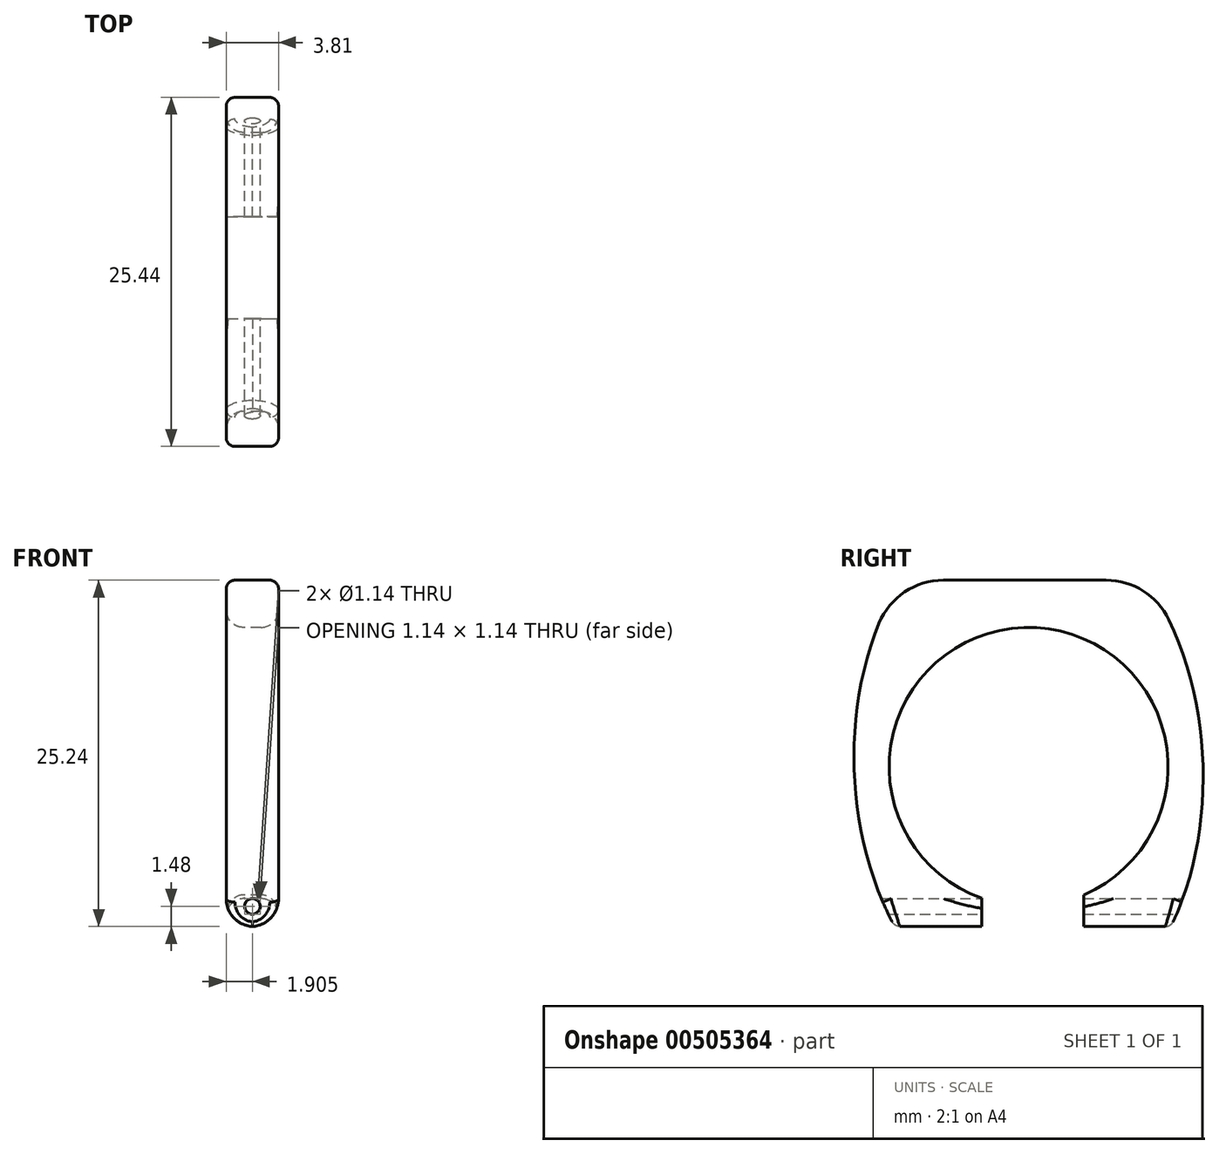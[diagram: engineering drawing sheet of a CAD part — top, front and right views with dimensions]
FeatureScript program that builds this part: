
annotation { "Feature Type Name" : "Feature", "Feature Type Description" : "" }
export const myFeature = defineFeature(function(context is Context, id is Id, definition is map)
    precondition{}
    {
        {
            var Q0;
            Q0=qCreatedBy(makeId("Right.planeOp"),FACE);
            var sketch = newSketch(context, id + "F0", { "sketchPlane" : qUnion([Q0])});
            skCircle(sketch, "E0", {"center": v(0, 10.16) * mm, "radius": 10.16 * mm});
            skEllipticalArc(sketch, "E1", {});
            skLineSegment(sketch, "E2", {"start": v(10.36, -1.48) * mm, "end": v(4.01, -1.48) * mm});
            skLineSegment(sketch, "E3", {"start": v(8.53, 23.76) * mm, "end": v(-9.25, 23.76) * mm});
            skCircle(sketch, "E4", {"center": v(0, 10.16) * mm, "radius": 0.64 * mm});
            skPoint(sketch, "E5", {"position": v(4.01, -1.48) * mm});
            skPoint(sketch, "E6", {"position": v(-3.4, -1.48) * mm});
            skLineSegment(sketch, "E7.trimOffspring", {"start": v(-3.4, -1.48) * mm, "end": v(-9.75, -1.48) * mm});
            skLineSegment(sketch, "E8", {"start": v(4.01, -1.48) * mm, "end": v(4.01, 0.83) * mm});
            skLineSegment(sketch, "E9", {"start": v(-3.4, -1.48) * mm, "end": v(-3.4, 0.59) * mm});
            const initialGuessF0  = {"E1": [0, 0.01016, -0.047142897118615544, 0.9988881555265653, 0.01905, 0.0127, 4.023068995079654, 2.197209903459385]};
            skSetInitialGuess(sketch, initialGuessF0);
            skSolve(sketch);
        }
        {
            var Q0;
            Q0=makeQuery(id+"F0.imprint","IMPRINT",FACE,{"disambiguationData":[TD([[makeQuery(id+"F0.imprint","IMPRINT",EDGE,{"derivedFrom":sQuery(id+"F0.wireOp",EDGE,"E0")}),-1.0]])]});
            extrude(context, id + "F1", {"entities" : qUnion([Q0]), "depth" : 3.8 * mm});
        }
        {
            var Q0;
            Q0=makeQuery(id+"F1.opExtrude","CAP_EDGE",EDGE,{"disambiguationData":[OSD([sQuery(id+"F0.wireOp",EDGE,"E0")])],"isStart":true});
            var Q1;
            Q1=makeQuery(id+"F1.opExtrude","CAP_EDGE",EDGE,{"disambiguationData":[OSD([sQuery(id+"F0.wireOp",EDGE,"E0")])],"isStart":false});
            fillet(context, id + "F2", {"entities" : qUnion([Q0, Q1]), "radius" : 1.27 * mm, "tangentPropagation" : true, "allowEdgeOverflow" : false});
        }
        {
            var Q0;
            Q0=qCreatedBy(makeId("Front.planeOp"),FACE);
            var sketch = newSketch(context, id + "F3", { "sketchPlane" : qUnion([Q0])});
            skCircle(sketch, "E10", {"center": v(1.9, 0) * mm, "radius": 0.57 * mm});
            skSolve(sketch);
        }
        {
            var Q0;
            Q0=makeQuery(id+"F3.imprint","IMPRINT",FACE,{"disambiguationData":[TD([[makeQuery(id+"F3.imprint","IMPRINT",EDGE,{"derivedFrom":sQuery(id+"F3.wireOp",EDGE,"E10")}),1.0]])]});
            extrude(context, id + "F4", {"entities" : qUnion([Q0]), "depth" : 101.6 * mm, "hasSecondDirection" : true, "secondDirectionOppositeDirection" : true, "secondDirectionDepth" : 101.6 * mm});
        }
        {
            var Q0;
            Q0=makeQuery(id+"F4.opExtrude","SWEPT_BODY",BODY,{"disambiguationData":[OSD([sQuery(id+"F3.wireOp",EDGE,"E10")])]});
            var Q1;
            Q1=makeQuery(id+"F1.opExtrude","SWEPT_BODY",BODY,{"disambiguationData":[OSD([sQuery(id+"F0.wireOp",EDGE,"E0"),sQuery(id+"F0.wireOp",EDGE,"E1"),sQuery(id+"F0.wireOp",EDGE,"E2"),sQuery(id+"F0.wireOp",EDGE,"E3")])]});
            booleanBodies(context, id + "F5", {"operationType" : BooleanOperationType.SUBTRACTION, "tools" : qUnion([Q0]), "targets" : qUnion([Q1])});
        }
        {
            var Q0;
            Q0=makeQuery(id+"F1.opExtrude","CAP_EDGE",EDGE,{"disambiguationData":[OSD([sQuery(id+"F0.wireOp",EDGE,"E2")])],"isStart":true});
            var Q1;
            Q1=makeQuery(id+"F1.opExtrude","CAP_EDGE",EDGE,{"disambiguationData":[OSD([sQuery(id+"F0.wireOp",EDGE,"E2")])],"isStart":false});
            var Q2;
            Q2=makeQuery(id+"F1.opExtrude","CAP_EDGE",EDGE,{"disambiguationData":[OSD([sQuery(id+"F0.wireOp",EDGE,"E7.trimOffspring")])],"isStart":false});
            var Q3;
            Q3=makeQuery(id+"F1.opExtrude","CAP_EDGE",EDGE,{"disambiguationData":[OSD([sQuery(id+"F0.wireOp",EDGE,"E7.trimOffspring")])],"isStart":true});
            fillet(context, id + "F6", {"entities" : qUnion([Q0, Q1, Q2, Q3]), "radius" : 2.03 * mm, "tangentPropagation" : true, "allowEdgeOverflow" : false});
        }
        {
            var Q0;
            {var subQ0=sQuery(id+"F0.wireOp",EDGE,"E1");Q0=makeQuery(id+"F1.opExtrude","CAP_EDGE",EDGE,{"disambiguationData":[OSD([subQ0]),TDD([makeQuery(id+"F0.imprint","IMPRINT",EDGE,{"disambiguationData":[TD([[makeQuery(id+"F0.imprint","INTERSECT",VERTEX,{"disambiguationData":[OD(0.0)],"derivedFrom":[subQ0,sQuery(id+"F0.wireOp",EDGE,"E3")]}),-1.0]])],"derivedFrom":subQ0})])],"isStart":false});}
            var Q1;
            {var subQ0=sQuery(id+"F0.wireOp",EDGE,"E1");Q1=makeQuery(id+"F1.opExtrude","CAP_EDGE",EDGE,{"disambiguationData":[OSD([subQ0]),TDD([makeQuery(id+"F0.imprint","IMPRINT",EDGE,{"disambiguationData":[TD([[makeQuery(id+"F0.imprint","INTERSECT",VERTEX,{"disambiguationData":[OD(0.0)],"derivedFrom":[subQ0,sQuery(id+"F0.wireOp",EDGE,"E3")]}),-1.0]])],"derivedFrom":subQ0})])],"isStart":true});}
            var Q2;
            {var subQ0=sQuery(id+"F0.wireOp",EDGE,"E1");Q2=makeQuery(id+"F1.opExtrude","CAP_EDGE",EDGE,{"disambiguationData":[OSD([subQ0]),TDD([makeQuery(id+"F0.imprint","IMPRINT",EDGE,{"disambiguationData":[TD([[makeQuery(id+"F0.imprint","INTERSECT",VERTEX,{"disambiguationData":[OD(0.0)],"derivedFrom":[subQ0,sQuery(id+"F0.wireOp",EDGE,"E2")]}),-1.0]])],"derivedFrom":subQ0})])],"isStart":false});}
            var Q3;
            {var subQ0=sQuery(id+"F0.wireOp",EDGE,"E1");Q3=makeQuery(id+"F1.opExtrude","CAP_EDGE",EDGE,{"disambiguationData":[OSD([subQ0]),TDD([makeQuery(id+"F0.imprint","IMPRINT",EDGE,{"disambiguationData":[TD([[makeQuery(id+"F0.imprint","INTERSECT",VERTEX,{"disambiguationData":[OD(0.0)],"derivedFrom":[subQ0,sQuery(id+"F0.wireOp",EDGE,"E2")]}),-1.0]])],"derivedFrom":subQ0})])],"isStart":true});}
            var Q4;
            Q4=makeQuery(id+"F1.opExtrude","CAP_EDGE",EDGE,{"disambiguationData":[OSD([sQuery(id+"F0.wireOp",EDGE,"E3")])],"isStart":false});
            var Q5;
            Q5=makeQuery(id+"F1.opExtrude","CAP_EDGE",EDGE,{"disambiguationData":[OSD([sQuery(id+"F0.wireOp",EDGE,"E3")])],"isStart":true});
            fillet(context, id + "F7", {"entities" : qUnion([Q0, Q1, Q2, Q3, Q4, Q5]), "radius" : 0.64 * mm, "tangentPropagation" : true, "allowEdgeOverflow" : false});
        }
        {
            var Q0;
            {var subQ0=sQuery(id+"F0.wireOp",EDGE,"E3");var subQ1=sQuery(id+"F0.wireOp",EDGE,"E1");Q0=makeQuery(id+"F1.opExtrude","SWEPT_EDGE",EDGE,{"disambiguationData":[OSD([subQ1,subQ0]),TDD([makeQuery(id+"F0.imprint","INTERSECT",VERTEX,{"disambiguationData":[OD(1.0)],"derivedFrom":[subQ1,subQ0]})])]});}
            var Q1;
            {var subQ0=sQuery(id+"F0.wireOp",EDGE,"E3");var subQ1=sQuery(id+"F0.wireOp",EDGE,"E1");Q1=makeQuery(id+"F1.opExtrude","SWEPT_EDGE",EDGE,{"disambiguationData":[OSD([subQ1,subQ0]),TDD([makeQuery(id+"F0.imprint","INTERSECT",VERTEX,{"disambiguationData":[OD(0.0)],"derivedFrom":[subQ1,subQ0]})])]});}
            fillet(context, id + "F8", {"entities" : qUnion([Q0, Q1]), "radius" : 5.08 * mm, "tangentPropagation" : true, "allowEdgeOverflow" : false});
        }
    });
